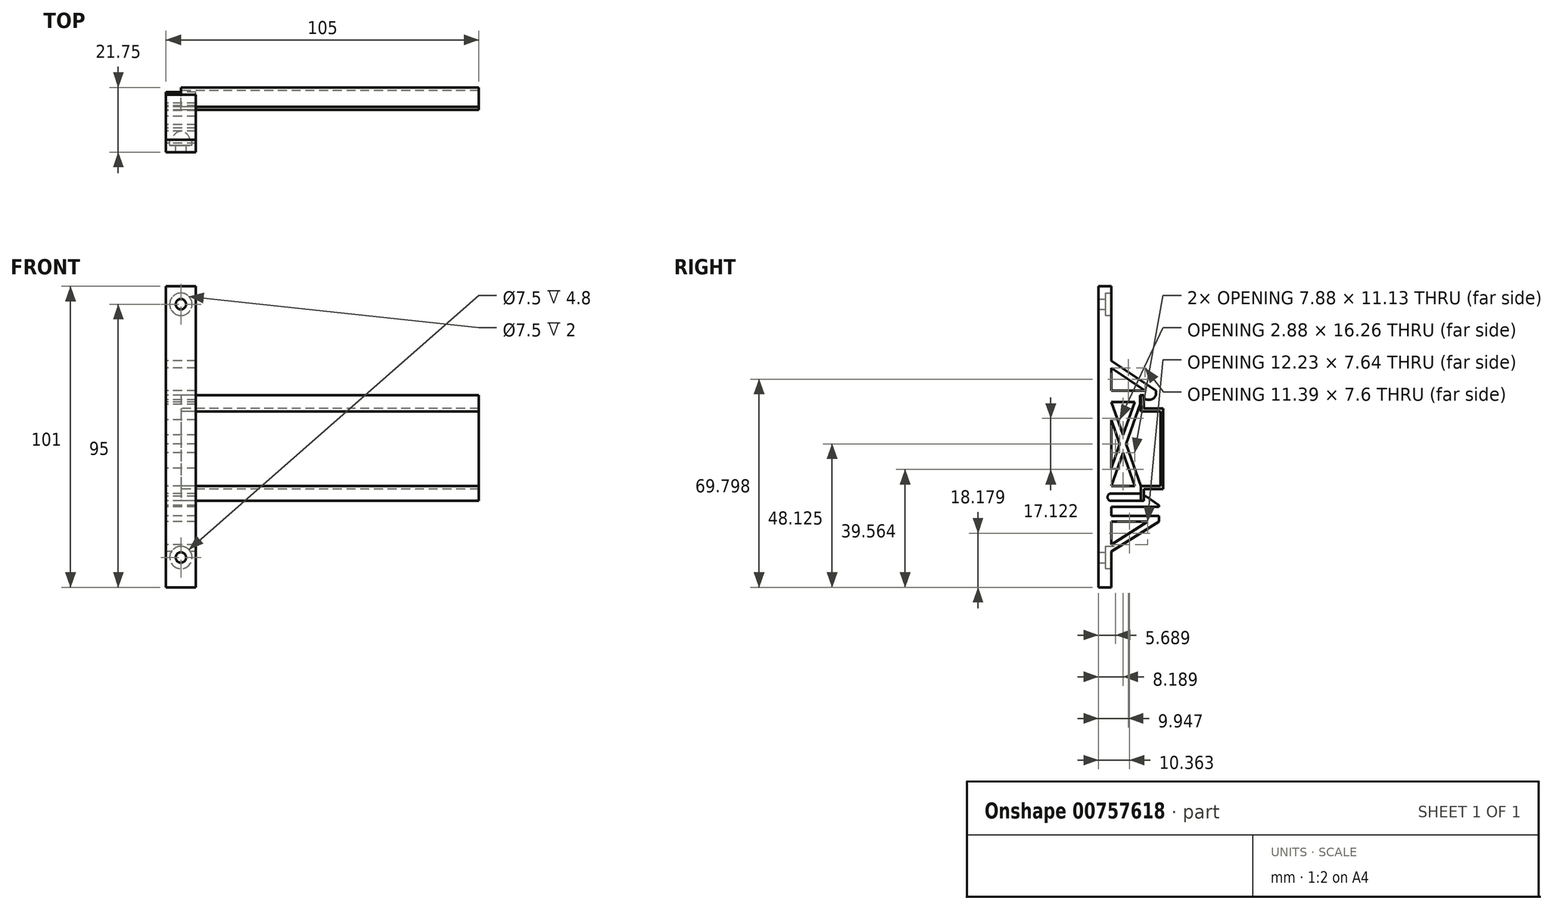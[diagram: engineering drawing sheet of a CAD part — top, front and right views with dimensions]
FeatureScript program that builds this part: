
annotation { "Feature Type Name" : "Feature", "Feature Type Description" : "" }
export const myFeature = defineFeature(function(context is Context, id is Id, definition is map)
    precondition{}
    {
        {
            var Q0;
            Q0=qCreatedBy(makeId("Right.planeOp"),FACE);
            var sketch = newSketch(context, id + "F0", { "sketchPlane" : qUnion([Q0])});
            skLineSegment(sketch, "E0", {"start": v(-6.5, 18) * mm, "end": v(-6.5, 12.5) * mm});
            skLineSegment(sketch, "E1", {"start": v(-6.5, 12.5) * mm, "end": v(0, 12.5) * mm});
            skLineSegment(sketch, "E2", {"start": v(0, 12.5) * mm, "end": v(0, -12.5) * mm});
            skLineSegment(sketch, "E3", {"start": v(0, -12.5) * mm, "end": v(-6.5, -12.5) * mm});
            skLineSegment(sketch, "E4", {"start": v(-6.5, -12.5) * mm, "end": v(-6.5, -17.5) * mm});
            skLineSegment(sketch, "E5.0", {"start": v(-5.5, -13.5) * mm, "end": v(-5.5, -17.5) * mm});
            skLineSegment(sketch, "E5.1", {"start": v(-5.5, 18) * mm, "end": v(-5.5, 13.5) * mm});
            skLineSegment(sketch, "E5.2", {"start": v(-5.5, 13.5) * mm, "end": v(1, 13.5) * mm});
            skLineSegment(sketch, "E5.3", {"start": v(1, 13.5) * mm, "end": v(1, -13.5) * mm});
            skLineSegment(sketch, "E5.4", {"start": v(1, -13.5) * mm, "end": v(-5.5, -13.5) * mm});
            skLineSegment(sketch, "E6", {"start": v(-6.5, 18) * mm, "end": v(-5.5, 18) * mm});
            skLineSegment(sketch, "E7", {"start": v(-6.5, -17.5) * mm, "end": v(-5.5, -17.5) * mm});
            skSolve(sketch);
        }
        {
            var Q0;
            Q0=makeQuery(id+"F0.imprint","IMPRINT",FACE,{"disambiguationData":[TD([[makeQuery(id+"F0.imprint","IMPRINT",EDGE,{"derivedFrom":sQuery(id+"F0.wireOp",EDGE,"E0")}),1.0]])]});
            extrude(context, id + "F1", {"entities" : qUnion([Q0]), "depth" : 100 * mm, "offsetDistance" : 25 * mm});
        }
        {
            var Q0;
            Q0=qCreatedBy(makeId("Right.planeOp"),FACE);
            var sketch = newSketch(context, id + "F2", { "sketchPlane" : qUnion([Q0])});
            skLineSegment(sketch, "E8.0.0", {"start": v(-5.5, 13.5) * mm, "end": v(-5.5, 18) * mm, "construction": true});
            skLineSegment(sketch, "E8.0.1", {"start": v(-5.5, 18) * mm, "end": v(-6.5, 18) * mm, "construction": true});
            skLineSegment(sketch, "E8.0.2", {"start": v(-6.5, 18) * mm, "end": v(-6.5, 12.5) * mm, "construction": true});
            skLineSegment(sketch, "E8.0.3", {"start": v(-6.5, 12.5) * mm, "end": v(0, 12.5) * mm, "construction": true});
            skLineSegment(sketch, "E8.0.4", {"start": v(0, 12.5) * mm, "end": v(0, -12.5) * mm, "construction": true});
            skLineSegment(sketch, "E8.0.5", {"start": v(0, -12.5) * mm, "end": v(-6.5, -12.5) * mm, "construction": true});
            skLineSegment(sketch, "E8.0.6", {"start": v(-6.5, -12.5) * mm, "end": v(-6.5, -17.5) * mm, "construction": true});
            skLineSegment(sketch, "E8.0.7", {"start": v(-6.5, -17.5) * mm, "end": v(-5.5, -17.5) * mm, "construction": true});
            skLineSegment(sketch, "E8.0.8", {"start": v(-5.5, -17.5) * mm, "end": v(-5.5, -13.5) * mm, "construction": true});
            skLineSegment(sketch, "E8.0.9", {"start": v(-5.5, -13.5) * mm, "end": v(1, -13.5) * mm, "construction": true});
            skLineSegment(sketch, "E8.0.10", {"start": v(1, -13.5) * mm, "end": v(1, 13.5) * mm, "construction": true});
            skLineSegment(sketch, "E8.0.11", {"start": v(1, 13.5) * mm, "end": v(-5.5, 13.5) * mm, "construction": true});
            skLineSegment(sketch, "E9", {"start": v(-1.5, 18.5) * mm, "end": v(-1.5, 19.5) * mm});
            skLineSegment(sketch, "E10", {"start": v(-1.5, 19.5) * mm, "end": v(-20.75, 19.5) * mm});
            skLineSegment(sketch, "E11", {"start": v(-4.71, -16.05) * mm, "end": v(-0.5, -19) * mm});
            skLineSegment(sketch, "E12", {"start": v(-0.5, -19) * mm, "end": v(-0.5, -19.5) * mm});
            skLineSegment(sketch, "E13", {"start": v(-0.5, -19.5) * mm, "end": v(-16.5, -19.5) * mm});
            skLineSegment(sketch, "E14", {"start": v(-16.5, -12.5) * mm, "end": v(-8.62, -12.5) * mm});
            skLineSegment(sketch, "E15", {"start": v(-6.5, -15) * mm, "end": v(-16.5, -15) * mm});
            skLineSegment(sketch, "E16", {"start": v(-6.5, -15) * mm, "end": v(-6.5, -12.5) * mm});
            skLineSegment(sketch, "E17", {"start": v(-5.5, -16.46) * mm, "end": v(-5.5, -17.5) * mm});
            skLineSegment(sketch, "E18", {"start": v(-16.5, -17.5) * mm, "end": v(-5.5, -17.5) * mm});
            skArc(sketch, "E19", {"start": v(-16.5, -15) * mm, "mid": v(-17.75, -16.25) * mm, "end": v(-16.5, -17.5) * mm});
            skLineSegment(sketch, "E20", {"start": v(-16.5, -19.5) * mm, "end": v(-20.75, -19.5) * mm});
            skLineSegment(sketch, "E21", {"start": v(-20.75, -19.5) * mm, "end": v(-20.75, 19.5) * mm});
            skLineSegment(sketch, "E22", {"start": v(-5.5, 16.5) * mm, "end": v(-5.5, 18) * mm});
            skLineSegment(sketch, "E23", {"start": v(-6.5, 18) * mm, "end": v(-6.5, 15.75) * mm, "construction": true});
            skLineSegment(sketch, "E24", {"start": v(-6.5, 15.75) * mm, "end": v(-8.62, 15.75) * mm, "construction": true});
            skLineSegment(sketch, "E25", {"start": v(-16.5, 15.75) * mm, "end": v(-16.5, -6.5) * mm});
            skLineSegment(sketch, "E26", {"start": v(-6.5, 18) * mm, "end": v(-5.5, 18) * mm});
            skLineSegment(sketch, "E27", {"start": v(-16.5, 15.75) * mm, "end": v(-11.5, 1.63) * mm});
            skLineSegment(sketch, "E28.0", {"start": v(-16.5, 9.76) * mm, "end": v(-16.5, 9.76) * mm});
            skLineSegment(sketch, "E29", {"start": v(-16.5, -12.5) * mm, "end": v(-11.5, 1.62) * mm});
            skLineSegment(sketch, "E30.0", {"start": v(-16.5, -6.5) * mm, "end": v(-13.62, 1.63) * mm});
            skLineSegment(sketch, "E31", {"start": v(-8.62, -12.5) * mm, "end": v(-6.5, -12.5) * mm, "construction": true});
            skLineSegment(sketch, "E32", {"start": v(-16.5, -6.5) * mm, "end": v(-16.5, -12.5) * mm, "construction": true});
            skLineSegment(sketch, "E33", {"start": v(-8.62, 15.75) * mm, "end": v(-16.5, 15.75) * mm});
            skLineSegment(sketch, "E34", {"start": v(-12.56, 4.62) * mm, "end": v(-8.62, 15.75) * mm});
            skLineSegment(sketch, "E35", {"start": v(-13.62, 1.63) * mm, "end": v(-12.56, 4.62) * mm, "construction": true});
            skLineSegment(sketch, "E36", {"start": v(-12.56, -1.37) * mm, "end": v(-8.62, -12.5) * mm});
            skLineSegment(sketch, "E37", {"start": v(-11.5, 1.62) * mm, "end": v(-6.5, 15.75) * mm});
            skLineSegment(sketch, "E38", {"start": v(-12.6, -1.23) * mm, "end": v(-12.56, -1.37) * mm});
            skLineSegment(sketch, "E39", {"start": v(-11.5, 1.63) * mm, "end": v(-6.5, -12.5) * mm});
            skLineSegment(sketch, "E40", {"start": v(-16.5, 9.76) * mm, "end": v(-12.6, -1.23) * mm});
            skLineSegment(sketch, "E41.0", {"start": v(-6.8, 18) * mm, "end": v(-6.8, 14.9) * mm});
            skLineSegment(sketch, "E42", {"start": v(-6.8, 18) * mm, "end": v(-6.5, 18) * mm});
            skPoint(sketch, "E43.visualSharp", {"position": v(-5.5, -15.5) * mm});
            skArc(sketch, "E43.filletArc", {"start": v(-4.71, -16.05) * mm, "mid": v(-5.23, -16.02) * mm, "end": v(-5.5, -16.46) * mm});
            skPoint(sketch, "E44.visualSharp", {"position": v(-5.5, 15.75) * mm});
            skLineSegment(sketch, "E45", {"start": v(-20.75, -19.5) * mm, "end": v(-20.75, -34.5) * mm});
            skLineSegment(sketch, "E46", {"start": v(-20.75, -34.5) * mm, "end": v(-16.5, -34.5) * mm});
            skLineSegment(sketch, "E47", {"start": v(-16.5, -34.5) * mm, "end": v(-0.5, -24.5) * mm});
            skLineSegment(sketch, "E48", {"start": v(-0.5, -24.5) * mm, "end": v(-0.5, -22.5) * mm});
            skLineSegment(sketch, "E49", {"start": v(-0.5, -22.5) * mm, "end": v(-16.5, -22.5) * mm});
            skLineSegment(sketch, "E50", {"start": v(-16.5, -22.5) * mm, "end": v(-16.5, -19.5) * mm});
            skLineSegment(sketch, "E51", {"start": v(-16.5, -24.5) * mm, "end": v(-16.5, -32.14) * mm});
            skLineSegment(sketch, "E52", {"start": v(-16.5, -32.14) * mm, "end": v(-4.27, -24.5) * mm});
            skLineSegment(sketch, "E53", {"start": v(-4.27, -24.5) * mm, "end": v(-16.5, -24.5) * mm});
            skLineSegment(sketch, "E54.bottom", {"start": v(-20.75, 19.5) * mm, "end": v(-16.5, 19.5) * mm});
            skLineSegment(sketch, "E54.top", {"start": v(-20.75, 54.5) * mm, "end": v(-16.5, 54.5) * mm});
            skLineSegment(sketch, "E54.left", {"start": v(-20.75, 19.5) * mm, "end": v(-20.75, 54.5) * mm});
            skLineSegment(sketch, "E54.right", {"start": v(-16.5, 19.5) * mm, "end": v(-16.5, 54.5) * mm});
            skLineSegment(sketch, "E55.bottom", {"start": v(-16.5, -34.5) * mm, "end": v(-20.75, -34.5) * mm});
            skLineSegment(sketch, "E55.top", {"start": v(-16.5, -46.5) * mm, "end": v(-20.75, -46.5) * mm});
            skLineSegment(sketch, "E55.left", {"start": v(-16.5, -34.5) * mm, "end": v(-16.5, -46.5) * mm});
            skLineSegment(sketch, "E55.right", {"start": v(-20.75, -34.5) * mm, "end": v(-20.75, -46.5) * mm});
            skLineSegment(sketch, "E56", {"start": v(-16.5, 48.5) * mm, "end": v(-20.75, 48.5) * mm, "construction": true});
            skLineSegment(sketch, "E57", {"start": v(-16.5, -36.5) * mm, "end": v(-20.75, -36.5) * mm, "construction": true});
            skLineSegment(sketch, "E58", {"start": v(-3.5, 16.5) * mm, "end": v(-4.5, 16.5) * mm});
            skLineSegment(sketch, "E59", {"start": v(-5.5, 17.5) * mm, "end": v(-5.5, 17.5) * mm});
            skLineSegment(sketch, "E60", {"start": v(-4.5, 16.5) * mm, "end": v(-5.5, 16.5) * mm, "construction": true});
            skArc(sketch, "E61", {"start": v(-5.5, 17.5) * mm, "mid": v(-5.2, 16.8) * mm, "end": v(-4.5, 16.5) * mm});
            skPoint(sketch, "E62.visualSharp", {"position": v(-1.5, 16.5) * mm});
            skArc(sketch, "E62.filletArc", {"start": v(-3.5, 16.5) * mm, "mid": v(-2.09, 17.09) * mm, "end": v(-1.5, 18.5) * mm});
            skLineSegment(sketch, "E63", {"start": v(-1.5, 19.5) * mm, "end": v(-16.5, 29.5) * mm});
            skLineSegment(sketch, "E64", {"start": v(-16.5, 27.1) * mm, "end": v(-5.1, 19.5) * mm});
            skSolve(sketch);
        }
        {
            var Q0;
            Q0=makeQuery(id+"F2.imprint","IMPRINT",FACE,{"disambiguationData":[TD([[makeQuery(id+"F2.imprint","IMPRINT",EDGE,{"derivedFrom":sQuery(id+"F2.wireOp",EDGE,"pd4Cvf8t-X5cX-jGJw-PlKc-imWmI2jFnaBs")}),1.0]])]});
            var Q1;
            {var subQ6=sQuery(id+"F2.wireOp",EDGE,"E38");Q1=makeQuery(id+"F2.imprint","IMPRINT",FACE,{"disambiguationData":[TD([[makeQuery(id+"F2.imprint","IMPRINT",EDGE,{"derivedFrom":subQ6}),1.0]])]});}
            var Q2;
            Q2=makeQuery(id+"F2.imprint","IMPRINT",FACE,{"disambiguationData":[TD([[makeQuery(id+"F2.imprint","IMPRINT",EDGE,{"derivedFrom":sQuery(id+"F2.wireOp",EDGE,"E20")}),1.0]])]});
            var Q3;
            {var subQ1=sQuery(id+"F2.wireOp",EDGE,"E54.top");Q3=makeQuery(id+"F2.imprint","IMPRINT",FACE,{"disambiguationData":[TD([[makeQuery(id+"F2.imprint","IMPRINT",EDGE,{"derivedFrom":subQ1}),-1.0]])]});}
            var Q4;
            Q4=makeQuery(id+"F2.imprint","IMPRINT",FACE,{"disambiguationData":[TD([[makeQuery(id+"F2.imprint","IMPRINT",EDGE,{"derivedFrom":sQuery(id+"F2.wireOp",EDGE,"E46")}),-1.0]])]});
            var Q5;
            {var subQ20=sQuery(id+"F2.wireOp",EDGE,"E9");Q5=makeQuery(id+"F2.imprint","IMPRINT",FACE,{"disambiguationData":[TD([[makeQuery(id+"F2.imprint","IMPRINT",EDGE,{"derivedFrom":subQ20}),1.0]])]});}
            var Q6;
            {var subQ0=sQuery(id+"F2.wireOp",EDGE,"E63");Q6=makeQuery(id+"F2.imprint","IMPRINT",FACE,{"disambiguationData":[TD([[makeQuery(id+"F2.imprint","IMPRINT",EDGE,{"derivedFrom":subQ0}),1.0]])]});}
            extrude(context, id + "F3", {"entities" : qUnion([Q0, Q1, Q2, Q3, Q4, Q5, Q6]), "endBound" : BoundingType.SYMMETRIC, "depth" : 10 * mm, "offsetDistance" : 25 * mm});
        }
        {
            var Q0;
            Q0=makeQuery(id+"F3.opExtrude","SWEPT_FACE",FACE,{"disambiguationData":[OSD([sQuery(id+"F2.wireOp",EDGE,"E9")])]});
            var sketch = newSketch(context, id + "F4", { "sketchPlane" : qUnion([Q0])});
            skPoint(sketch, "E65.0", {"position": v(0, 48.5) * mm});
            skPoint(sketch, "E66.0", {"position": v(0, -36.5) * mm});
            skSolve(sketch);
        }
        {
            var Q0;
            Q0=sQuery(id+"F4.wireOp",VERTEX,"E65.1");
            var Q1;
            Q1=sQuery(id+"F4.wireOp",VERTEX,"E65.0");
            var Q2;
            Q2=sQuery(id+"F4.wireOp",VERTEX,"E66.0");
            var Q3;
            Q3=makeQuery(id+"F3.opExtrude","SWEPT_BODY",BODY,{"disambiguationData":[OSD([sQuery(id+"F2.wireOp",EDGE,"E9"),sQuery(id+"F2.wireOp",EDGE,"E10"),sQuery(id+"F2.wireOp",EDGE,"E11"),sQuery(id+"F2.wireOp",EDGE,"E12"),sQuery(id+"F2.wireOp",EDGE,"E13"),sQuery(id+"F2.wireOp",EDGE,"E14"),sQuery(id+"F2.wireOp",EDGE,"E15"),sQuery(id+"F2.wireOp",EDGE,"E16"),sQuery(id+"F2.wireOp",EDGE,"E17"),sQuery(id+"F2.wireOp",EDGE,"E18"),sQuery(id+"F2.wireOp",EDGE,"E19"),sQuery(id+"F2.wireOp",EDGE,"E21"),sQuery(id+"F2.wireOp",EDGE,"E22"),sQuery(id+"F2.wireOp",EDGE,"E25"),sQuery(id+"F2.wireOp",EDGE,"E26"),sQuery(id+"F2.wireOp",EDGE,"E27"),sQuery(id+"F2.wireOp",EDGE,"E29"),sQuery(id+"F2.wireOp",EDGE,"E30.0"),sQuery(id+"F2.wireOp",EDGE,"E33"),sQuery(id+"F2.wireOp",EDGE,"E34"),sQuery(id+"F2.wireOp",EDGE,"E36"),sQuery(id+"F2.wireOp",EDGE,"E37"),sQuery(id+"F2.wireOp",EDGE,"E39"),sQuery(id+"F2.wireOp",EDGE,"E40"),sQuery(id+"F2.wireOp",EDGE,"E41.0"),sQuery(id+"F2.wireOp",EDGE,"E42"),sQuery(id+"F2.wireOp",EDGE,"E43.filletArc"),sQuery(id+"F2.wireOp",EDGE,"E45"),sQuery(id+"F2.wireOp",EDGE,"E47"),sQuery(id+"F2.wireOp",EDGE,"E48"),sQuery(id+"F2.wireOp",EDGE,"E49"),sQuery(id+"F2.wireOp",EDGE,"E50"),sQuery(id+"F2.wireOp",EDGE,"E51"),sQuery(id+"F2.wireOp",EDGE,"E52"),sQuery(id+"F2.wireOp",EDGE,"E53"),sQuery(id+"F2.wireOp",EDGE,"E54.top"),sQuery(id+"F2.wireOp",EDGE,"E54.left"),sQuery(id+"F2.wireOp",EDGE,"E54.right"),sQuery(id+"F2.wireOp",EDGE,"E55.top"),sQuery(id+"F2.wireOp",EDGE,"E55.left"),sQuery(id+"F2.wireOp",EDGE,"E55.right"),sQuery(id+"F2.wireOp",EDGE,"E58"),sQuery(id+"F2.wireOp",EDGE,"E61"),sQuery(id+"F2.wireOp",EDGE,"E62.filletArc"),sQuery(id+"F2.wireOp",EDGE,"E63"),sQuery(id+"F2.wireOp",EDGE,"E64")])]});
            hole(context, id + "F5", {"style" : HoleStyle.C_BORE, "endStyle" : HoleEndStyle.THROUGH, "standardTappedOrClearance" : lookupTablePath({ "standard" : "ISO", "size" : "3.5", "type" : "Drilled" }), "standardBlindInLast" : lookupTablePath({ "standard" : "ISO", "size" : "3.5", "type" : "Drilled" }), "holeDiameter" : 3.5 * mm, "cBoreDiameter" : 7.5 * mm, "cBoreDepth" : 17 * mm, "majorDiameter" : 5 * mm, "isTappedThrough" : true, "tappedDepth" : 12 * mm, "tapClearance" : 3, "startFromSketch" : true, "locations" : qUnion([Q0, Q1, Q2]), "scope" : qUnion([Q3])});
        }
    });
